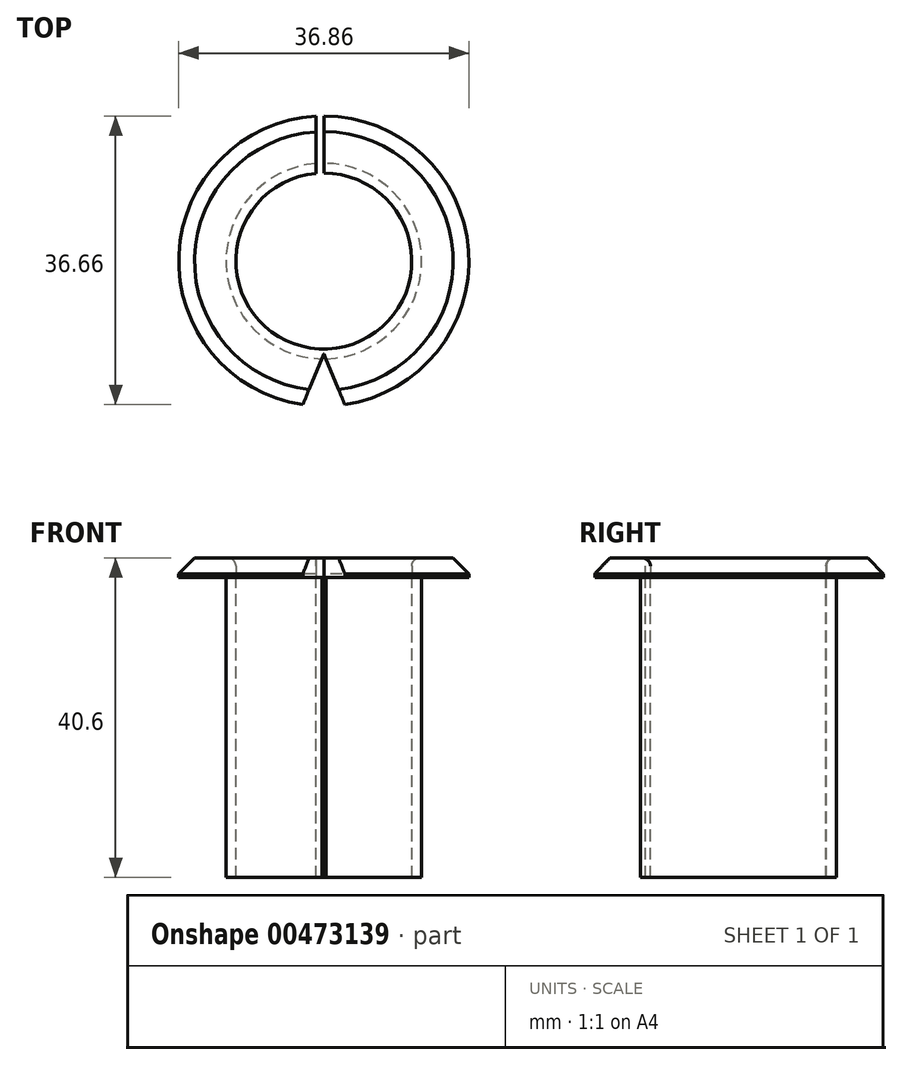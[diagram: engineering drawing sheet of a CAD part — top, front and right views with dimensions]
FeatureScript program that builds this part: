
annotation { "Feature Type Name" : "Feature", "Feature Type Description" : "" }
export const myFeature = defineFeature(function(context is Context, id is Id, definition is map)
    precondition{}
    {
        {
            var Q0;
            Q0=qCreatedBy(makeId("Top.planeOp"),FACE);
            var sketch = newSketch(context, id + "F0", { "sketchPlane" : qUnion([Q0])});
            skCircle(sketch, "E0", {"center": v(0, 0) * mm, "radius": 11.18 * mm});
            skCircle(sketch, "E1", {"center": v(0, 0) * mm, "radius": 18.43 * mm});
            skCircle(sketch, "E2", {"center": v(0, 0) * mm, "radius": 12.43 * mm});
            skSolve(sketch);
        }
        {
            var Q0;
            Q0=makeQuery(id+"F0.imprint","IMPRINT",FACE,{"disambiguationData":[TD([[makeQuery(id+"F0.imprint","IMPRINT",EDGE,{"derivedFrom":sQuery(id+"F0.wireOp",EDGE,"E0")}),-1.0]])]});
            extrude(context, id + "F1", {"entities" : qUnion([Q0]), "oppositeDirection" : true, "depth" : 38.1 * mm});
        }
        {
            var Q0;
            Q0=makeQuery(id+"F0.imprint","IMPRINT",FACE,{"disambiguationData":[TD([[makeQuery(id+"F0.imprint","IMPRINT",EDGE,{"derivedFrom":sQuery(id+"F0.wireOp",EDGE,"E0")}),-1.0]])]});
            var Q1;
            Q1=makeQuery(id+"F0.imprint","IMPRINT",FACE,{"disambiguationData":[TD([[makeQuery(id+"F0.imprint","IMPRINT",EDGE,{"derivedFrom":sQuery(id+"F0.wireOp",EDGE,"E1")}),1.0]])]});
            extrude(context, id + "F2", {"entities" : qUnion([Q0, Q1]), "depth" : 2.5 * mm});
        }
        {
            var Q0;
            Q0=makeQuery(id+"F2.opExtrude","CAP_EDGE",EDGE,{"disambiguationData":[OSD([sQuery(id+"F0.wireOp",EDGE,"E1")])],"isStart":false});
            chamfer(context, id + "F3", {"entities" : qUnion([Q0]), "width" : 2 * mm, "tangentPropagation" : true});
        }
        {
            var Q0;
            Q0=makeQuery(id+"F2.opExtrude","CAP_EDGE",EDGE,{"disambiguationData":[OSD([sQuery(id+"F0.wireOp",EDGE,"E0")])],"isStart":false});
            fillet(context, id + "F4", {"entities" : qUnion([Q0]), "radius" : 1 * mm, "tangentPropagation" : true, "allowEdgeOverflow" : false});
        }
        {
            var Q0;
            Q0=qCreatedBy(makeId("Right.planeOp"),FACE);
            var sketch = newSketch(context, id + "F5", { "sketchPlane" : qUnion([Q0])});
            skLineSegment(sketch, "E3.bottom", {"start": v(0, 10.57) * mm, "end": v(26.7, 10.57) * mm});
            skLineSegment(sketch, "E3.top", {"start": v(0, -45.57) * mm, "end": v(26.7, -45.57) * mm});
            skLineSegment(sketch, "E3.left", {"start": v(0, 10.57) * mm, "end": v(0, -45.57) * mm});
            skLineSegment(sketch, "E3.right", {"start": v(26.7, 10.57) * mm, "end": v(26.7, -45.57) * mm});
            skSolve(sketch);
        }
        {
            var Q0;
            Q0=makeQuery(id+"F5.imprint","IMPRINT",FACE,{"disambiguationData":[TD([[makeQuery(id+"F5.imprint","IMPRINT",EDGE,{"derivedFrom":sQuery(id+"F5.wireOp",EDGE,"E3.bottom")}),-1.0]])]});
            extrude(context, id + "F6", {"entities" : qUnion([Q0]), "operationType" : NewBodyOperationType.REMOVE, "oppositeDirection" : true, "depth" : 1 * mm});
        }
        {
            var Q0;
            Q0=qCreatedBy(makeId("Top.planeOp"),FACE);
            var sketch = newSketch(context, id + "F7", { "sketchPlane" : qUnion([Q0])});
            skLineSegment(sketch, "E4", {"start": v(0, -11.8) * mm, "end": v(-5.74, -25.67) * mm});
            skLineSegment(sketch, "E5.MirrorCS", {"start": v(0, -11.8) * mm, "end": v(5.74, -25.67) * mm});
            skLineSegment(sketch, "E6", {"start": v(-5.74, -25.67) * mm, "end": v(5.74, -25.67) * mm});
            skSolve(sketch);
        }
        {
            var Q0;
            Q0 = qSketchRegion(id + "F7", true);
            extrude(context, id + "F8", {"entities" : qUnion([Q0]), "operationType" : NewBodyOperationType.REMOVE, "endBound" : BoundingType.SYMMETRIC, "oppositeDirection" : true, "depth" : 100 * mm});
        }
    });
